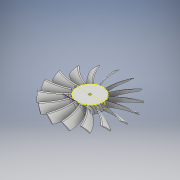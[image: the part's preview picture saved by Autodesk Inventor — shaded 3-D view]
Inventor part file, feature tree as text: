
AUTODESK INVENTOR PART (.ipt)
format: ipt  version: 2018 (Build 220112000, 112)  size: 2,792,960 bytes
history: native  units: mm
features: sketch x7, extrude x4, pattern_circular x3, plane x2, fillet x2, sweep x1, projected_geometry x1
ambient origin geometry x8: Origin, YZ Plane, XZ Plane, XY Plane, X Axis, Y Axis, Z Axis, Center Point
bodies: Solid1 (feature_tree)
feature tree (20):
  extrude  "Extrusion1"  Depth=25.0mm
  sketch  "Sketch2"  dims[d3=2.0mm d4=2.0mm]
  plane  "Work Plane1"
  sweep  "Sweep1"
  extrude  "Extrusion2"  Depth=4.363323mm TaperAngle=0.0deg
  pattern_circular  "Circular Pattern1"  Count=16 Angle=360.0deg
  plane  "Work Plane3"
  extrude  "Extrusion3"  Depth=5.0mm TaperAngle=0.0deg
  extrude  "Extrusion4"  Depth=10.0mm TaperAngle=0.0deg
  fillet  "Fillet2"  Radius=2.0mm
  pattern_circular  "Circular Pattern2"  Count=16 Angle=360.0deg
  fillet  "Fillet3"  Radius=160.0mm
  pattern_circular  "Circular Pattern3"  [2 undecoded]
  sketch  "Sketch1"  dims[d0=2.1mm d1=25.0mm]
  sketch  "Sketch3"  dims[d5=8.0mm d6=0.0mm d14=0.0mm d15=4.363323mm]
  sketch  "Sketch5"  dims[d16=1.0mm d17=0.0mm d18=160.0mm d19=360.0deg]
  sketch  "Sketch6"  dims[d21=12.5mm d22=5.0mm d23=0.0mm]
  sketch  "Sketch9"  dims[d25=25.0mm d26=10.0mm d27=0.0mm d30=2.0mm d31=160.0mm d32=360.0deg d34=2.0mm d35=160.0mm d36=360.0deg]
  projected_geometry  "Projected Loop3"
  sketch  "Sketch10"
note: 2 required parameter values undecoded (feature->parameter linkage not recoverable at this tier; creation-order binding heuristic only, values carry confidence <= 0.55)
